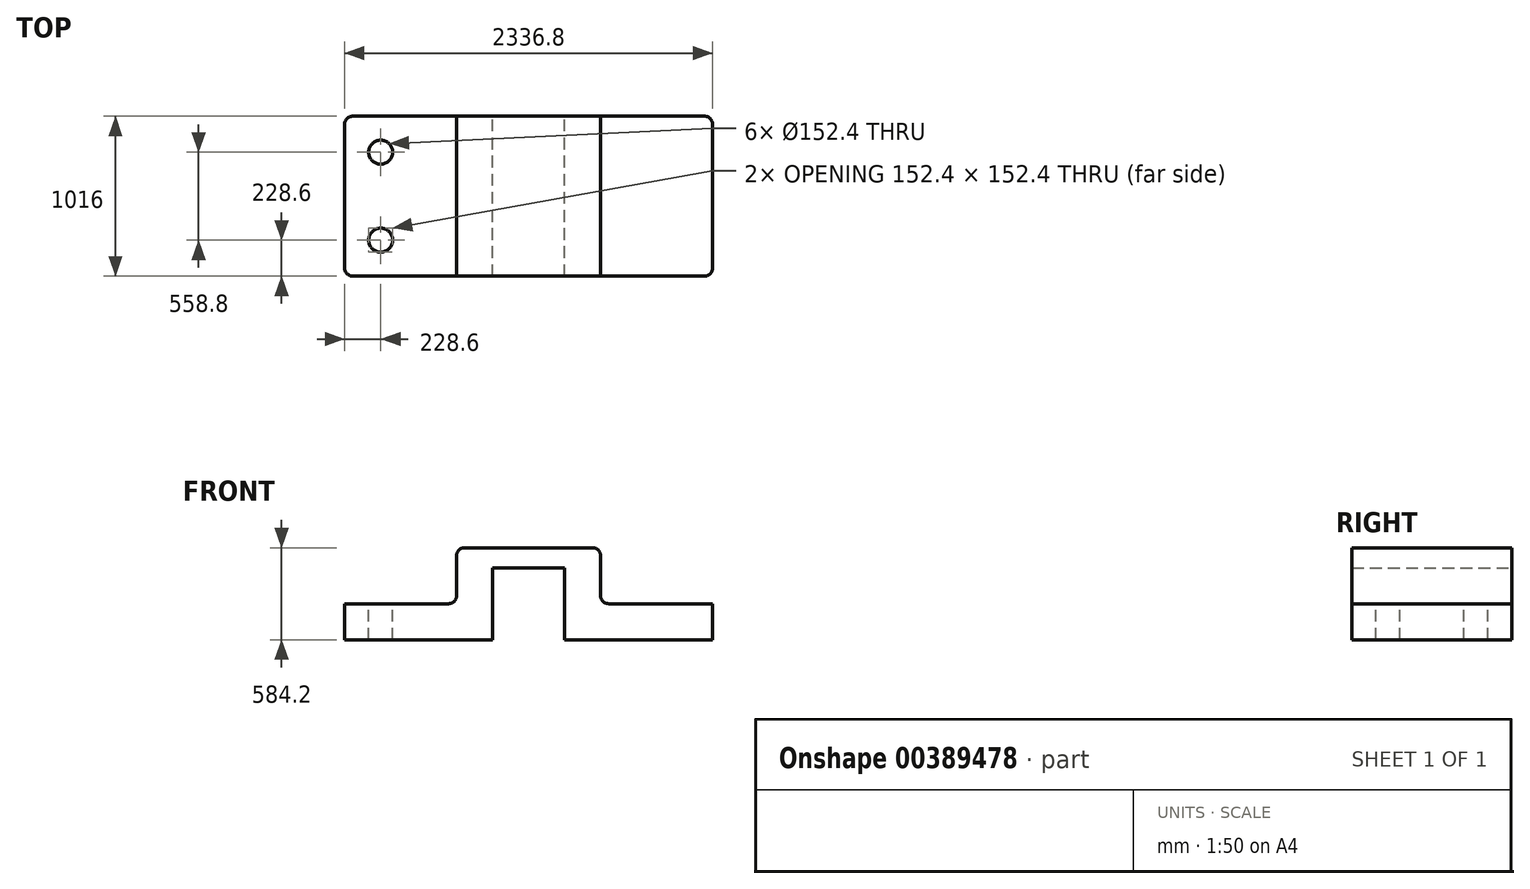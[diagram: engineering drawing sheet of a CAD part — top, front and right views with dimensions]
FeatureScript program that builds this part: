
annotation { "Feature Type Name" : "Feature", "Feature Type Description" : "" }
export const myFeature = defineFeature(function(context is Context, id is Id, definition is map)
    precondition{}
    {
        {
            var Q0;
            Q0=qCreatedBy(makeId("Front.planeOp"),FACE);
            var sketch = newSketch(context, id + "F0", { "sketchPlane" : qUnion([Q0])});
            skLineSegment(sketch, "E0", {"start": v(0, 0) * mm, "end": v(-939.8, 0) * mm});
            skLineSegment(sketch, "E1", {"start": v(-2336.8, 0) * mm, "end": v(-2336.8, 228.6) * mm});
            skLineSegment(sketch, "E2", {"start": v(-2336.8, 228.6) * mm, "end": v(-1625.6, 228.6) * mm});
            skLineSegment(sketch, "E3", {"start": v(0, 0) * mm, "end": v(0, 228.6) * mm});
            skLineSegment(sketch, "E4", {"start": v(0, 228.6) * mm, "end": v(-711.2, 228.6) * mm});
            skLineSegment(sketch, "E5", {"start": v(-711.2, 228.6) * mm, "end": v(-711.2, 584.2) * mm});
            skLineSegment(sketch, "E6", {"start": v(-711.2, 584.2) * mm, "end": v(-1625.6, 584.2) * mm});
            skLineSegment(sketch, "E7", {"start": v(-1625.6, 584.2) * mm, "end": v(-1625.6, 228.6) * mm});
            skLineSegment(sketch, "E8", {"start": v(-1397, 228.6) * mm, "end": v(-1397, 0) * mm});
            skLineSegment(sketch, "E9", {"start": v(-1397, 228.6) * mm, "end": v(-1397, 457.2) * mm});
            skLineSegment(sketch, "E10", {"start": v(-939.8, 228.6) * mm, "end": v(-939.8, 0) * mm});
            skLineSegment(sketch, "E11", {"start": v(-939.8, 228.6) * mm, "end": v(-939.8, 457.2) * mm});
            skLineSegment(sketch, "E12", {"start": v(-1397, 457.2) * mm, "end": v(-939.8, 457.2) * mm});
            skPoint(sketch, "E13.orphan", {"position": v(-1625.6, 457.2) * mm});
            skLineSegment(sketch, "E14.trimOffspring", {"start": v(-1397, 0) * mm, "end": v(-2336.8, 0) * mm});
            skSolve(sketch);
        }
        {
            var Q0;
            Q0 = qSketchRegion(id + "F0", true);
            var Q1;
            Q1=makeQuery(id+"F0.imprint","IMPRINT",FACE,{"disambiguationData":[TD([[makeQuery(id+"F0.imprint","IMPRINT",EDGE,{"derivedFrom":sQuery(id+"F0.wireOp",EDGE,"E0")}),-1.0]])]});
            extrude(context, id + "F1", {"entities" : qUnion([Q0, Q1]), "depth" : 1016 * mm});
        }
        {
            var Q0;
            Q0=makeQuery(id+"F1.opExtrude","CAP_EDGE",EDGE,{"disambiguationData":[OSD([sQuery(id+"F0.wireOp",EDGE,"E3")])],"isStart":false});
            fillet(context, id + "F2", {"entities" : qUnion([Q0]), "radius" : 50.8 * mm, "tangentPropagation" : true, "allowEdgeOverflow" : false});
        }
        {
            var Q0;
            Q0=makeQuery(id+"F1.opExtrude","CAP_EDGE",EDGE,{"disambiguationData":[OSD([sQuery(id+"F0.wireOp",EDGE,"E3")])],"isStart":true});
            var Q1;
            Q1=makeQuery(id+"F1.opExtrude","SWEPT_EDGE",EDGE,{"disambiguationData":[OSD([sQuery(id+"F0.wireOp",EDGE,"E4"),sQuery(id+"F0.wireOp",EDGE,"E5")])]});
            var Q2;
            Q2=makeQuery(id+"F1.opExtrude","SWEPT_EDGE",EDGE,{"disambiguationData":[OSD([sQuery(id+"F0.wireOp",EDGE,"E5"),sQuery(id+"F0.wireOp",EDGE,"E6")])]});
            var Q3;
            Q3=makeQuery(id+"F1.opExtrude","SWEPT_EDGE",EDGE,{"disambiguationData":[OSD([sQuery(id+"F0.wireOp",EDGE,"E6"),sQuery(id+"F0.wireOp",EDGE,"E7")])]});
            var Q4;
            Q4=makeQuery(id+"F1.opExtrude","SWEPT_EDGE",EDGE,{"disambiguationData":[OSD([sQuery(id+"F0.wireOp",EDGE,"E2"),sQuery(id+"F0.wireOp",EDGE,"E7")])]});
            var Q5;
            Q5=makeQuery(id+"F1.opExtrude","CAP_EDGE",EDGE,{"disambiguationData":[OSD([sQuery(id+"F0.wireOp",EDGE,"E1")])],"isStart":true});
            var Q6;
            Q6=makeQuery(id+"F1.opExtrude","CAP_EDGE",EDGE,{"disambiguationData":[OSD([sQuery(id+"F0.wireOp",EDGE,"E1")])],"isStart":false});
            fillet(context, id + "F3", {"entities" : qUnion([Q0, Q1, Q2, Q3, Q4, Q5, Q6]), "radius" : 50.8 * mm, "tangentPropagation" : true, "allowEdgeOverflow" : false});
        }
        {
            var Q0;
            Q0=makeQuery(id+"F1.opExtrude","SWEPT_FACE",FACE,{"disambiguationData":[OSD([sQuery(id+"F0.wireOp",EDGE,"E2")])]});
            var sketch = newSketch(context, id + "F4", { "sketchPlane" : qUnion([Q0])});
            skCircle(sketch, "E15", {"center": v(-2108.2, -228.6) * mm, "radius": 76.2 * mm});
            skCircle(sketch, "E16", {"center": v(-2108.2, -787.4) * mm, "radius": 76.2 * mm});
            skLineSegment(sketch, "E17", {"start": v(-1168.4, 114.45) * mm, "end": v(-1168.4, -674.24) * mm});
            skCircle(sketch, "E18.MirrorC", {"center": v(-228.6, -228.6) * mm, "radius": 76.2 * mm});
            skCircle(sketch, "E19.MirrorC", {"center": v(-228.6, -787.4) * mm, "radius": 76.2 * mm});
            skSolve(sketch);
        }
        {
            var Q0;
            Q0=makeQuery(id+"F4.imprint","IMPRINT",FACE,{"disambiguationData":[TD([[makeQuery(id+"F4.imprint","IMPRINT",EDGE,{"derivedFrom":sQuery(id+"F4.wireOp",EDGE,"E18.MirrorC")}),-1.0]])]});
            var Q1;
            Q1=makeQuery(id+"F4.imprint","IMPRINT",FACE,{"disambiguationData":[TD([[makeQuery(id+"F4.imprint","IMPRINT",EDGE,{"derivedFrom":sQuery(id+"F4.wireOp",EDGE,"E19.MirrorC")}),-1.0]])]});
            var Q2;
            Q2=makeQuery(id+"F4.imprint","IMPRINT",FACE,{"disambiguationData":[TD([[makeQuery(id+"F4.imprint","IMPRINT",EDGE,{"derivedFrom":sQuery(id+"F4.wireOp",EDGE,"E16")}),1.0]])]});
            var Q3;
            Q3=makeQuery(id+"F4.imprint","IMPRINT",FACE,{"disambiguationData":[TD([[makeQuery(id+"F4.imprint","IMPRINT",EDGE,{"derivedFrom":sQuery(id+"F4.wireOp",EDGE,"E15")}),1.0]])]});
            extrude(context, id + "F5", {"entities" : qUnion([Q0, Q1, Q2, Q3]), "operationType" : NewBodyOperationType.REMOVE, "oppositeDirection" : true, "depth" : 2286 * mm});
        }
    });
